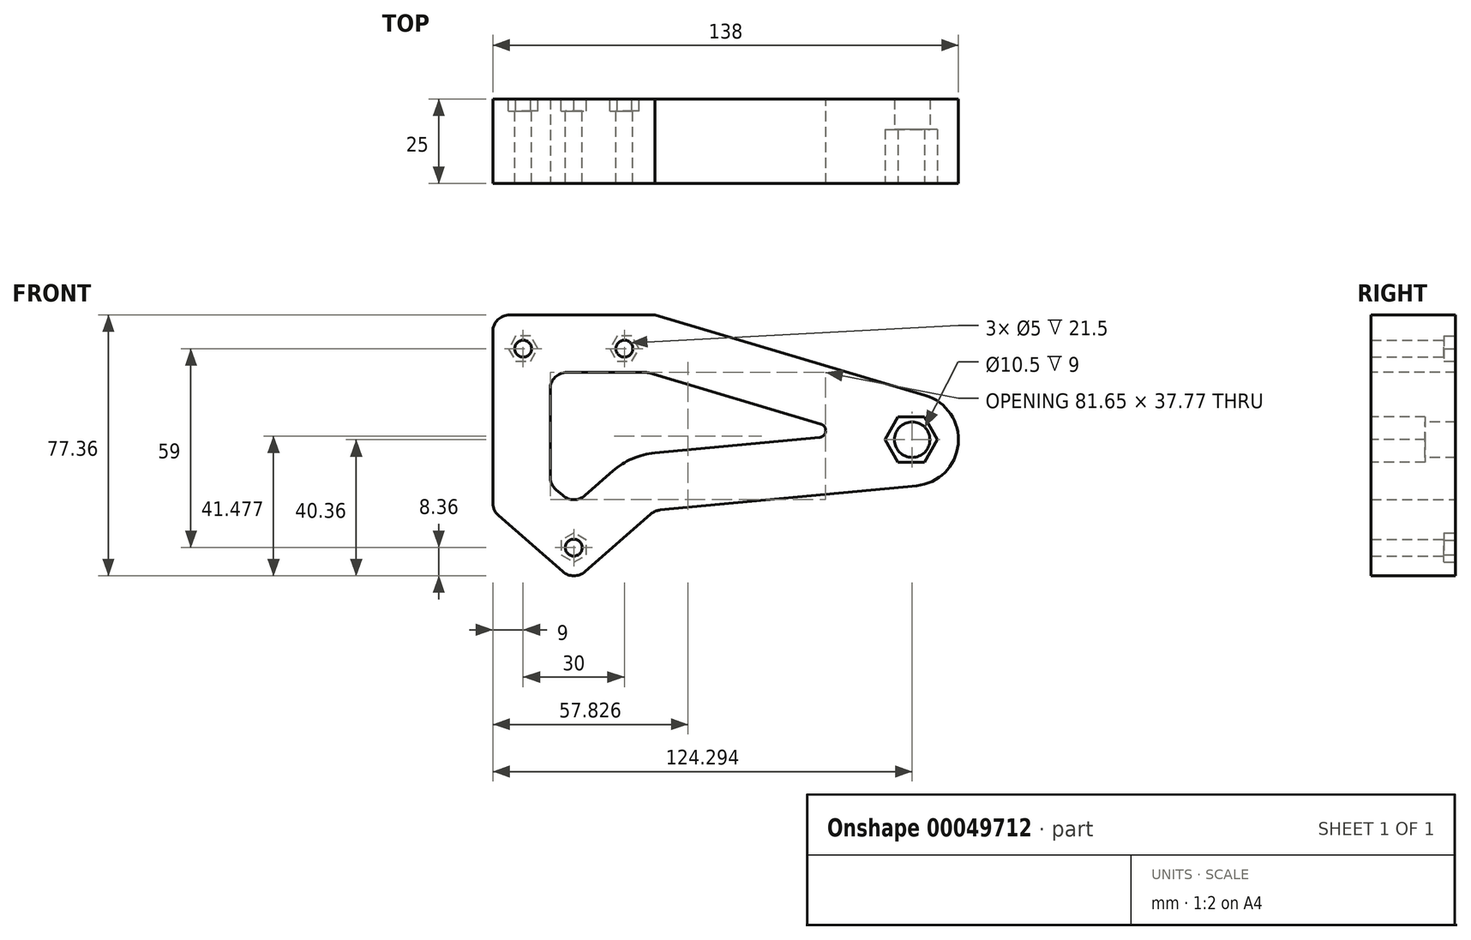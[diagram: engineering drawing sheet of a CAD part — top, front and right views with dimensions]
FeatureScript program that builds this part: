
annotation { "Feature Type Name" : "Feature", "Feature Type Description" : "" }
export const myFeature = defineFeature(function(context is Context, id is Id, definition is map)
    precondition{}
    {
        {
            var Q0;
            Q0=qCreatedBy(makeId("Front.planeOp"),FACE);
            var sketch = newSketch(context, id + "F0", { "sketchPlane" : qUnion([Q0])});
            skLineSegment(sketch, "E0", {"start": v(-24, 29) * mm, "end": v(24, 29) * mm});
            skLineSegment(sketch, "E1", {"start": v(24, 29) * mm, "end": v(24, -29) * mm});
            skLineSegment(sketch, "E2", {"start": v(24, -29) * mm, "end": v(-24, -29) * mm});
            skLineSegment(sketch, "E3", {"start": v(-24, -29) * mm, "end": v(-24, 29) * mm});
            skLineSegment(sketch, "E4", {"start": v(-24, -29) * mm, "end": v(0, -50) * mm});
            skLineSegment(sketch, "E5", {"start": v(0, -50) * mm, "end": v(24, -29) * mm});
            skLineSegment(sketch, "E6", {"start": v(24, 29) * mm, "end": v(114, 29) * mm});
            skLineSegment(sketch, "E7", {"start": v(114, 29) * mm, "end": v(114, -29) * mm});
            skLineSegment(sketch, "E8", {"start": v(114, -29) * mm, "end": v(24, -29) * mm});
            skCircle(sketch, "E9", {"center": v(-15, 19) * mm, "radius": 2.5 * mm});
            skCircle(sketch, "E10", {"center": v(15, 19) * mm, "radius": 2.5 * mm});
            skCircle(sketch, "E11", {"center": v(0, -40) * mm, "radius": 2.5 * mm});
            skSolve(sketch);
        }
        {
            var Q0;
            Q0=makeQuery(id+"F0.imprint","IMPRINT",FACE,{"disambiguationData":[TD([[makeQuery(id+"F0.imprint","IMPRINT",EDGE,{"derivedFrom":sQuery(id+"F0.wireOp",EDGE,"E0")}),-1.0]])]});
            var Q1;
            Q1=makeQuery(id+"F0.imprint","IMPRINT",FACE,{"disambiguationData":[TD([[makeQuery(id+"F0.imprint","IMPRINT",EDGE,{"derivedFrom":sQuery(id+"F0.wireOp",EDGE,"E1")}),1.0]])]});
            var Q2;
            Q2=makeQuery(id+"F0.imprint","IMPRINT",FACE,{"disambiguationData":[TD([[makeQuery(id+"F0.imprint","IMPRINT",EDGE,{"derivedFrom":sQuery(id+"F0.wireOp",EDGE,"E2")}),1.0]])]});
            extrude(context, id + "F1", {"entities" : qUnion([Q0, Q1, Q2]), "depth" : 25 * mm});
        }
        {
            var Q0;
            Q0=makeQuery(id+"F1.opExtrude","CAP_FACE",FACE,{"disambiguationData":[OSD([sQuery(id+"F0.wireOp",EDGE,"E0"),sQuery(id+"F0.wireOp",EDGE,"E3"),sQuery(id+"F0.wireOp",EDGE,"E4"),sQuery(id+"F0.wireOp",EDGE,"E5"),sQuery(id+"F0.wireOp",EDGE,"E6"),sQuery(id+"F0.wireOp",EDGE,"E7"),sQuery(id+"F0.wireOp",EDGE,"E8")])],"isStart":false});
            var sketch = newSketch(context, id + "F2", { "sketchPlane" : qUnion([Q0])});
            skCircle(sketch, "E12.cCircle", {"center": v(100, -8) * mm, "radius": 6.75 * mm, "construction": true});
            skLineSegment(sketch, "E12.0", {"start": v(103.9, -14.75) * mm, "end": v(96.1, -14.75) * mm});
            skLineSegment(sketch, "E12.1", {"start": v(96.1, -14.75) * mm, "end": v(92.2, -8) * mm});
            skLineSegment(sketch, "E12.2", {"start": v(92.2, -8) * mm, "end": v(96.1, -1.25) * mm});
            skLineSegment(sketch, "E12.3", {"start": v(96.1, -1.25) * mm, "end": v(103.9, -1.25) * mm});
            skLineSegment(sketch, "E12.4", {"start": v(103.9, -1.25) * mm, "end": v(107.8, -8) * mm});
            skLineSegment(sketch, "E12.5", {"start": v(107.8, -8) * mm, "end": v(103.9, -14.75) * mm});
            skPoint(sketch, "E12.0.midPoint", {"position": v(100, -14.75) * mm});
            skSolve(sketch);
        }
        {
            var Q0;
            Q0=makeQuery(id+"F2.imprint","IMPRINT",FACE,{"disambiguationData":[TD([[makeQuery(id+"F2.imprint","IMPRINT",EDGE,{"derivedFrom":sQuery(id+"F2.wireOp",EDGE,"E12.0")}),-1.0]])]});
            extrude(context, id + "F3", {"entities" : qUnion([Q0]), "operationType" : NewBodyOperationType.REMOVE, "oppositeDirection" : true, "depth" : 16 * mm});
        }
        {
            var Q0;
            Q0=makeQuery(id+"F3.boolean.opBoolean","COPY",FACE,{"derivedFrom":makeQuery(id+"F3.opExtrude","CAP_FACE",FACE,{"disambiguationData":[OSD([sQuery(id+"F2.wireOp",EDGE,"E12.0"),sQuery(id+"F2.wireOp",EDGE,"E12.1"),sQuery(id+"F2.wireOp",EDGE,"E12.2"),sQuery(id+"F2.wireOp",EDGE,"E12.3"),sQuery(id+"F2.wireOp",EDGE,"E12.4"),sQuery(id+"F2.wireOp",EDGE,"E12.5")])],"isStart":false})});
            var sketch = newSketch(context, id + "F4", { "sketchPlane" : qUnion([Q0])});
            skLineSegment(sketch, "E13.0", {"start": v(96.1, -14.75) * mm, "end": v(92.2, -8) * mm});
            skLineSegment(sketch, "E14.0", {"start": v(107.8, -8) * mm, "end": v(103.9, -14.75) * mm});
            skPoint(sketch, "E15", {"position": v(100.3, -8) * mm});
            skLineSegment(sketch, "E16.0", {"start": v(96.1, -1.25) * mm, "end": v(103.9, -1.25) * mm});
            skLineSegment(sketch, "E17.0", {"start": v(103.9, -14.75) * mm, "end": v(96.1, -14.75) * mm});
            skSolve(sketch);
        }
        {
            var Q0;
            Q0=sQuery(id+"F4.wireOp",VERTEX,"E15");
            var Q1;
            Q1=makeQuery(id+"F1.opExtrude","SWEPT_BODY",BODY,{"disambiguationData":[OSD([sQuery(id+"F0.wireOp",EDGE,"E0"),sQuery(id+"F0.wireOp",EDGE,"E3"),sQuery(id+"F0.wireOp",EDGE,"E4"),sQuery(id+"F0.wireOp",EDGE,"E5"),sQuery(id+"F0.wireOp",EDGE,"E6"),sQuery(id+"F0.wireOp",EDGE,"E7"),sQuery(id+"F0.wireOp",EDGE,"E8")])]});
            hole(context, id + "F5", {"style" : HoleStyle.SIMPLE, "holeDiameter" : 10.5 * mm, "endStyle" : HoleEndStyle.THROUGH, "locations" : qUnion([Q0]), "scope" : qUnion([Q1])});
        }
        {
            var Q0;
            Q0=makeQuery(id+"F1.opExtrude","CAP_FACE",FACE,{"disambiguationData":[OSD([sQuery(id+"F0.wireOp",EDGE,"E0"),sQuery(id+"F0.wireOp",EDGE,"E3"),sQuery(id+"F0.wireOp",EDGE,"E4"),sQuery(id+"F0.wireOp",EDGE,"E5"),sQuery(id+"F0.wireOp",EDGE,"E6"),sQuery(id+"F0.wireOp",EDGE,"E7"),sQuery(id+"F0.wireOp",EDGE,"E8"),sQuery(id+"F0.wireOp",EDGE,"E9"),sQuery(id+"F0.wireOp",EDGE,"E10"),sQuery(id+"F0.wireOp",EDGE,"E11")])],"isStart":false});
            var sketch = newSketch(context, id + "F6", { "sketchPlane" : qUnion([Q0])});
            skLineSegment(sketch, "E18", {"start": v(24, 29) * mm, "end": v(104.2, 5.14) * mm});
            skCircle(sketch, "E19.0", {"center": v(100.3, -8) * mm, "radius": 5.25 * mm});
            skArc(sketch, "E20", {"start": v(101.59, -21.64) * mm, "mid": v(113.94, -9.33) * mm, "end": v(104.2, 5.14) * mm});
            skLineSegment(sketch, "E21", {"start": v(24, -29) * mm, "end": v(101.59, -21.64) * mm});
            skSolve(sketch);
        }
        {
            var Q0;
            {var subQ0=sQuery(id+"F6.wireOp",EDGE,"E18");Q0=makeQuery(id+"F6.imprint","IMPRINT",FACE,{"disambiguationData":[TD([[makeQuery(id+"F6.imprint","IMPRINT",EDGE,{"derivedFrom":subQ0}),1.0]])]});}
            var Q1;
            {var subQ0=sQuery(id+"F6.wireOp",EDGE,"E21");Q1=makeQuery(id+"F6.imprint","IMPRINT",FACE,{"disambiguationData":[TD([[makeQuery(id+"F6.imprint","IMPRINT",EDGE,{"derivedFrom":subQ0}),-1.0]])]});}
            extrude(context, id + "F7", {"entities" : qUnion([Q0, Q1]), "operationType" : NewBodyOperationType.REMOVE, "oppositeDirection" : true, "depth" : 25 * mm});
        }
        {
            var Q0;
            Q0=makeQuery(id+"F1.opExtrude","CAP_FACE",FACE,{"disambiguationData":[OSD([sQuery(id+"F0.wireOp",EDGE,"E0"),sQuery(id+"F0.wireOp",EDGE,"E3"),sQuery(id+"F0.wireOp",EDGE,"E4"),sQuery(id+"F0.wireOp",EDGE,"E5"),sQuery(id+"F0.wireOp",EDGE,"E6"),sQuery(id+"F0.wireOp",EDGE,"E7"),sQuery(id+"F0.wireOp",EDGE,"E8"),sQuery(id+"F0.wireOp",EDGE,"E9"),sQuery(id+"F0.wireOp",EDGE,"E10"),sQuery(id+"F0.wireOp",EDGE,"E11")])],"isStart":true});
            var sketch = newSketch(context, id + "F8", { "sketchPlane" : qUnion([Q0])});
            skCircle(sketch, "E22.0", {"center": v(-15, 19) * mm, "radius": 2.5 * mm});
            skCircle(sketch, "E23.0", {"center": v(15, 19) * mm, "radius": 2.5 * mm});
            skCircle(sketch, "E24.0", {"center": v(0, -40) * mm, "radius": 2.5 * mm});
            skCircle(sketch, "E25.cCircle", {"center": v(15, 19) * mm, "radius": 3.75 * mm, "construction": true});
            skLineSegment(sketch, "E25.0", {"start": v(17.17, 15.25) * mm, "end": v(12.83, 15.25) * mm});
            skLineSegment(sketch, "E25.1", {"start": v(12.83, 15.25) * mm, "end": v(10.67, 19) * mm});
            skLineSegment(sketch, "E25.2", {"start": v(10.67, 19) * mm, "end": v(12.83, 22.75) * mm});
            skLineSegment(sketch, "E25.3", {"start": v(12.83, 22.75) * mm, "end": v(17.17, 22.75) * mm});
            skLineSegment(sketch, "E25.4", {"start": v(17.17, 22.75) * mm, "end": v(19.33, 19) * mm});
            skLineSegment(sketch, "E25.5", {"start": v(19.33, 19) * mm, "end": v(17.17, 15.25) * mm});
            skPoint(sketch, "E25.0.midPoint", {"position": v(15, 15.25) * mm});
            skCircle(sketch, "E26.cCircle", {"center": v(0, -40) * mm, "radius": 3.75 * mm, "construction": true});
            skLineSegment(sketch, "E26.0", {"start": v(0, -44.33) * mm, "end": v(-3.75, -42.17) * mm});
            skLineSegment(sketch, "E26.1", {"start": v(-3.75, -42.17) * mm, "end": v(-3.75, -37.83) * mm});
            skLineSegment(sketch, "E26.2", {"start": v(-3.75, -37.83) * mm, "end": v(0, -35.67) * mm});
            skLineSegment(sketch, "E26.3", {"start": v(0, -35.67) * mm, "end": v(3.75, -37.83) * mm});
            skLineSegment(sketch, "E26.4", {"start": v(3.75, -37.83) * mm, "end": v(3.75, -42.17) * mm});
            skLineSegment(sketch, "E26.5", {"start": v(3.75, -42.17) * mm, "end": v(0, -44.33) * mm});
            skPoint(sketch, "E26.0.midPoint", {"position": v(-1.88, -43.25) * mm});
            skCircle(sketch, "E27.cCircle", {"center": v(-15, 19) * mm, "radius": 3.75 * mm, "construction": true});
            skLineSegment(sketch, "E27.0", {"start": v(-12.83, 15.25) * mm, "end": v(-17.17, 15.25) * mm});
            skLineSegment(sketch, "E27.1", {"start": v(-17.17, 15.25) * mm, "end": v(-19.33, 19) * mm});
            skLineSegment(sketch, "E27.2", {"start": v(-19.33, 19) * mm, "end": v(-17.17, 22.75) * mm});
            skLineSegment(sketch, "E27.3", {"start": v(-17.17, 22.75) * mm, "end": v(-12.83, 22.75) * mm});
            skLineSegment(sketch, "E27.4", {"start": v(-12.83, 22.75) * mm, "end": v(-10.67, 19) * mm});
            skLineSegment(sketch, "E27.5", {"start": v(-10.67, 19) * mm, "end": v(-12.83, 15.25) * mm});
            skPoint(sketch, "E27.0.midPoint", {"position": v(-15, 15.25) * mm});
            skSolve(sketch);
        }
        {
            var Q0;
            Q0=makeQuery(id+"F8.imprint","IMPRINT",FACE,{"disambiguationData":[TD([[makeQuery(id+"F8.imprint","IMPRINT",EDGE,{"derivedFrom":sQuery(id+"F8.wireOp",EDGE,"E23.0")}),1.0]])]});
            var Q1;
            Q1=makeQuery(id+"F8.imprint","IMPRINT",FACE,{"disambiguationData":[TD([[makeQuery(id+"F8.imprint","IMPRINT",EDGE,{"derivedFrom":sQuery(id+"F8.wireOp",EDGE,"E22.0")}),1.0]])]});
            var Q2;
            Q2=makeQuery(id+"F8.imprint","IMPRINT",FACE,{"disambiguationData":[TD([[makeQuery(id+"F8.imprint","IMPRINT",EDGE,{"derivedFrom":sQuery(id+"F8.wireOp",EDGE,"E24.0")}),1.0]])]});
            extrude(context, id + "F9", {"entities" : qUnion([Q0, Q1, Q2]), "operationType" : NewBodyOperationType.REMOVE, "oppositeDirection" : true, "depth" : 3.5 * mm});
        }
        {
            var Q0;
            Q0=makeQuery(id+"F1.opExtrude","SWEPT_EDGE",EDGE,{"disambiguationData":[OSD([sQuery(id+"F0.wireOp",EDGE,"E0"),sQuery(id+"F0.wireOp",EDGE,"E3")])]});
            var Q1;
            Q1=makeQuery(id+"F7.boolean.opBoolean","COPY",EDGE,{"derivedFrom":makeQuery(id+"F7.opExtrude","SWEPT_EDGE",EDGE,{"disambiguationData":[OSD([sQuery(id+"F0.wireOp",EDGE,"E0"),sQuery(id+"F0.wireOp",EDGE,"E6"),sQuery(id+"F6.wireOp",EDGE,"E18")])]})});
            var Q2;
            Q2=makeQuery(id+"F1.opExtrude","SWEPT_EDGE",EDGE,{"disambiguationData":[OSD([sQuery(id+"F0.wireOp",EDGE,"E2"),sQuery(id+"F0.wireOp",EDGE,"E3"),sQuery(id+"F0.wireOp",EDGE,"E4")])]});
            var Q3;
            Q3=makeQuery(id+"F1.opExtrude","SWEPT_EDGE",EDGE,{"disambiguationData":[OSD([sQuery(id+"F0.wireOp",EDGE,"E4"),sQuery(id+"F0.wireOp",EDGE,"E5")])]});
            var Q4;
            {var subQ0=sQuery(id+"F0.wireOp",EDGE,"E8");var subQ1=sQuery(id+"F0.wireOp",EDGE,"E5");Q4=makeQuery(id+"F7.boolean.opBoolean","MERGE",EDGE,{"derivedFrom":[makeQuery(id+"F1.opExtrude","SWEPT_EDGE",EDGE,{"disambiguationData":[OSD([sQuery(id+"F0.wireOp",EDGE,"E1"),sQuery(id+"F0.wireOp",EDGE,"E2"),subQ1,subQ0])]}),makeQuery(id+"F7.opExtrude","SWEPT_EDGE",EDGE,{"disambiguationData":[OSD([subQ1,subQ0,sQuery(id+"F6.wireOp",EDGE,"E21")])]})]});}
            fillet(context, id + "F10", {"entities" : qUnion([Q0, Q1, Q2, Q3, Q4]), "radius" : 5 * mm, "tangentPropagation" : true, "allowEdgeOverflow" : false});
        }
        {
            var Q0;
            Q0=makeQuery(id+"F1.opExtrude","CAP_FACE",FACE,{"disambiguationData":[OSD([sQuery(id+"F0.wireOp",EDGE,"E0"),sQuery(id+"F0.wireOp",EDGE,"E3"),sQuery(id+"F0.wireOp",EDGE,"E4"),sQuery(id+"F0.wireOp",EDGE,"E5"),sQuery(id+"F0.wireOp",EDGE,"E6"),sQuery(id+"F0.wireOp",EDGE,"E7"),sQuery(id+"F0.wireOp",EDGE,"E8"),sQuery(id+"F0.wireOp",EDGE,"E9"),sQuery(id+"F0.wireOp",EDGE,"E10"),sQuery(id+"F0.wireOp",EDGE,"E11")])],"isStart":false});
            var sketch = newSketch(context, id + "F11", { "sketchPlane" : qUnion([Q0])});
            skLineSegment(sketch, "E28.0.0", {"start": v(104.2, 5.14) * mm, "end": v(24.7, 28.8) * mm});
            skArc(sketch, "E28.0.1", {"start": v(24.7, 28.8) * mm, "mid": v(24, 28.95) * mm, "end": v(23.27, 29) * mm});
            skLineSegment(sketch, "E28.0.2", {"start": v(23.27, 29) * mm, "end": v(-19, 29) * mm});
            skArc(sketch, "E28.0.3", {"start": v(-19, 29) * mm, "mid": v(-22.54, 27.54) * mm, "end": v(-24, 24) * mm});
            skLineSegment(sketch, "E28.0.4", {"start": v(-24, 24) * mm, "end": v(-24, -26.73) * mm});
            skArc(sketch, "E28.0.5", {"start": v(-24, -26.73) * mm, "mid": v(-23.55, -28.8) * mm, "end": v(-22.3, -30.5) * mm});
            skLineSegment(sketch, "E28.0.6", {"start": v(-22.3, -30.5) * mm, "end": v(-3.3, -47.12) * mm});
            skArc(sketch, "E28.0.7", {"start": v(-3.3, -47.12) * mm, "mid": v(0, -48.36) * mm, "end": v(3.3, -47.12) * mm});
            skLineSegment(sketch, "E28.0.8", {"start": v(3.3, -47.12) * mm, "end": v(22.79, -30.06) * mm});
            skArc(sketch, "E28.0.9", {"start": v(22.79, -30.06) * mm, "mid": v(24.1, -29.23) * mm, "end": v(25.6, -28.85) * mm});
            skLineSegment(sketch, "E28.0.10", {"start": v(25.6, -28.85) * mm, "end": v(101.59, -21.64) * mm});
            skArc(sketch, "E28.0.11", {"start": v(101.59, -21.64) * mm, "mid": v(113.94, -9.33) * mm, "end": v(104.2, 5.14) * mm});
            skLineSegment(sketch, "E29.1", {"start": v(24, -11.92) * mm, "end": v(83.1, -6.32) * mm});
            skLineSegment(sketch, "E29.2", {"start": v(83.1, -6.32) * mm, "end": v(21.52, 12) * mm});
            skArc(sketch, "E29.3", {"start": v(11.6, -17.27) * mm, "mid": v(17.38, -13.62) * mm, "end": v(24, -11.92) * mm});
            skLineSegment(sketch, "E29.4", {"start": v(21.52, 12) * mm, "end": v(-7, 12) * mm});
            skLineSegment(sketch, "E29.5", {"start": v(-7, 12) * mm, "end": v(-7, -21.29) * mm});
            skLineSegment(sketch, "E29.6", {"start": v(-7, -21.29) * mm, "end": v(0, -27.41) * mm});
            skLineSegment(sketch, "E29.7", {"start": v(0, -27.41) * mm, "end": v(11.6, -17.27) * mm});
            skSolve(sketch);
        }
        {
            var Q0;
            Q0=makeQuery(id+"F11.imprint","IMPRINT",FACE,{"disambiguationData":[TD([[makeQuery(id+"F11.imprint","IMPRINT",EDGE,{"derivedFrom":sQuery(id+"F11.wireOp",EDGE,"E29.1")}),1.0]])]});
            extrude(context, id + "F12", {"entities" : qUnion([Q0]), "operationType" : NewBodyOperationType.REMOVE, "endBound" : BoundingType.THROUGH_ALL, "oppositeDirection" : true, "depth" : 25 * mm});
        }
        {
            var Q0;
            Q0=makeQuery(id+"F12.boolean.opBoolean","COPY",EDGE,{"derivedFrom":makeQuery(id+"F12.opExtrude","SWEPT_EDGE",EDGE,{"disambiguationData":[OSD([sQuery(id+"F11.wireOp",EDGE,"E29.4"),sQuery(id+"F11.wireOp",EDGE,"E29.5")])]})});
            var Q1;
            Q1=makeQuery(id+"F12.boolean.opBoolean","COPY",EDGE,{"derivedFrom":makeQuery(id+"F12.opExtrude","SWEPT_EDGE",EDGE,{"disambiguationData":[OSD([sQuery(id+"F11.wireOp",EDGE,"E29.2"),sQuery(id+"F11.wireOp",EDGE,"E29.4")])]})});
            var Q2;
            Q2=makeQuery(id+"F12.boolean.opBoolean","COPY",EDGE,{"derivedFrom":makeQuery(id+"F12.opExtrude","SWEPT_EDGE",EDGE,{"disambiguationData":[OSD([sQuery(id+"F11.wireOp",EDGE,"E29.6"),sQuery(id+"F11.wireOp",EDGE,"E29.7")])]})});
            var Q3;
            Q3=makeQuery(id+"F12.boolean.opBoolean","COPY",EDGE,{"derivedFrom":makeQuery(id+"F12.opExtrude","SWEPT_EDGE",EDGE,{"disambiguationData":[OSD([sQuery(id+"F11.wireOp",EDGE,"E29.5"),sQuery(id+"F11.wireOp",EDGE,"E29.6")])]})});
            fillet(context, id + "F13", {"entities" : qUnion([Q0, Q1, Q2, Q3]), "radius" : 5 * mm, "tangentPropagation" : true, "allowEdgeOverflow" : false});
        }
        {
            var Q0;
            Q0=makeQuery(id+"F12.boolean.opBoolean","COPY",EDGE,{"derivedFrom":makeQuery(id+"F12.opExtrude","SWEPT_EDGE",EDGE,{"disambiguationData":[OSD([sQuery(id+"F11.wireOp",EDGE,"E29.1"),sQuery(id+"F11.wireOp",EDGE,"E29.2")])]})});
            fillet(context, id + "F14", {"entities" : qUnion([Q0]), "radius" : 2 * mm, "tangentPropagation" : true, "allowEdgeOverflow" : false});
        }
    });
